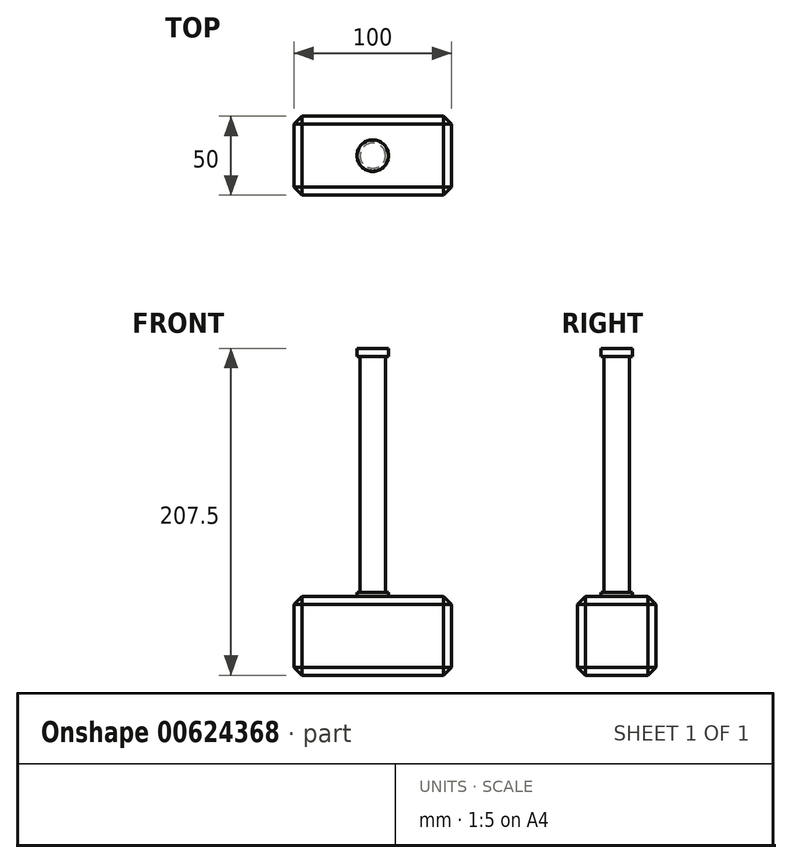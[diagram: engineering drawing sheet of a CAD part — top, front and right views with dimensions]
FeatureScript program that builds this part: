
annotation { "Feature Type Name" : "Feature", "Feature Type Description" : "" }
export const myFeature = defineFeature(function(context is Context, id is Id, definition is map)
    precondition{}
    {
        {
            var Q0;
            Q0=qCreatedBy(makeId("Top.planeOp"),FACE);
            var sketch = newSketch(context, id + "F0", { "sketchPlane" : qUnion([Q0])});
            skCircle(sketch, "E0", {"center": v(0, 0) * mm, "radius": 10.02 * mm});
            skSolve(sketch);
        }
        {
            var Q0;
            Q0 = qSketchRegion(id + "F0", true);
            extrude(context, id + "F1", {"entities" : qUnion([Q0]), "depth" : 2.5 * mm, "offsetDistance" : 25.4 * mm});
        }
        {
            var Q0;
            Q0=makeQuery(id+"F1.opExtrude","CAP_FACE",FACE,{"disambiguationData":[OSD([sQuery(id+"F0.wireOp",EDGE,"E0")])],"isStart":false});
            var sketch = newSketch(context, id + "F2", { "sketchPlane" : qUnion([Q0])});
            skCircle(sketch, "E1", {"center": v(0, 0) * mm, "radius": 8.04 * mm});
            skSolve(sketch);
        }
        {
            var Q0;
            Q0 = qSketchRegion(id + "F2", true);
            extrude(context, id + "F3", {"entities" : qUnion([Q0]), "operationType" : NewBodyOperationType.ADD, "depth" : 150 * mm, "offsetDistance" : 25.4 * mm});
        }
        {
            var Q0;
            Q0=makeQuery(id+"F3.opExtrude","CAP_FACE",FACE,{"disambiguationData":[OSD([sQuery(id+"F2.wireOp",EDGE,"E1")])],"isStart":false});
            var sketch = newSketch(context, id + "F4", { "sketchPlane" : qUnion([Q0])});
            skCircle(sketch, "E2", {"center": v(0, 0) * mm, "radius": 9.97 * mm});
            skSolve(sketch);
        }
        {
            var Q0;
            Q0=qCreatedBy(makeId("Top.planeOp"),FACE);
            var sketch = newSketch(context, id + "F5", { "sketchPlane" : qUnion([Q0])});
            skLineSegment(sketch, "E3.bottom", {"start": v(-50, 25) * mm, "end": v(50, 25) * mm});
            skLineSegment(sketch, "E3.top", {"start": v(-50, -25) * mm, "end": v(50, -25) * mm});
            skLineSegment(sketch, "E3.left", {"start": v(-50, 25) * mm, "end": v(-50, -25) * mm});
            skLineSegment(sketch, "E3.right", {"start": v(50, 25) * mm, "end": v(50, -25) * mm});
            skSolve(sketch);
        }
        {
            var Q0;
            Q0 = qSketchRegion(id + "F4", true);
            extrude(context, id + "F6", {"entities" : qUnion([Q0]), "operationType" : NewBodyOperationType.ADD, "depth" : 5 * mm, "offsetDistance" : 25.4 * mm});
        }
        {
            var Q0;
            Q0=makeQuery(id+"F5.imprint","IMPRINT",FACE,{"disambiguationData":[TD([[makeQuery(id+"F5.imprint","IMPRINT",EDGE,{"derivedFrom":sQuery(id+"F5.wireOp",EDGE,"E3.bottom")}),-1.0]])]});
            var Q1;
            Q1 = qSketchRegion(id + "F5", true);
            extrude(context, id + "F7", {"entities" : qUnion([Q0, Q1]), "operationType" : NewBodyOperationType.ADD, "oppositeDirection" : true, "depth" : 50 * mm, "offsetDistance" : 25.4 * mm});
        }
        {
            var Q0;
            Q0=makeQuery(id+"F7.opExtrude","SWEPT_FACE",FACE,{"disambiguationData":[OSD([sQuery(id+"F5.wireOp",EDGE,"E3.top")])]});
            var Q1;
            Q1=makeQuery(id+"F7.opExtrude","SWEPT_FACE",FACE,{"disambiguationData":[OSD([sQuery(id+"F5.wireOp",EDGE,"E3.bottom")])]});
            var Q2;
            Q2=makeQuery(id+"F7.opExtrude","CAP_FACE",FACE,{"disambiguationData":[OSD([sQuery(id+"F5.wireOp",EDGE,"E3.bottom"),sQuery(id+"F5.wireOp",EDGE,"E3.top"),sQuery(id+"F5.wireOp",EDGE,"E3.left"),sQuery(id+"F5.wireOp",EDGE,"E3.right")])],"isStart":false});
            var Q3;
            Q3=makeQuery(id+"F7.opExtrude","SWEPT_FACE",FACE,{"disambiguationData":[OSD([sQuery(id+"F5.wireOp",EDGE,"E3.right")])]});
            var Q4;
            Q4=makeQuery(id+"F7.opExtrude","SWEPT_FACE",FACE,{"disambiguationData":[OSD([sQuery(id+"F5.wireOp",EDGE,"E3.left")])]});
            chamfer(context, id + "F8", {"entities" : qUnion([Q0, Q1, Q2, Q3, Q4]), "width" : 5.08 * mm, "tangentPropagation" : true});
        }
    });
